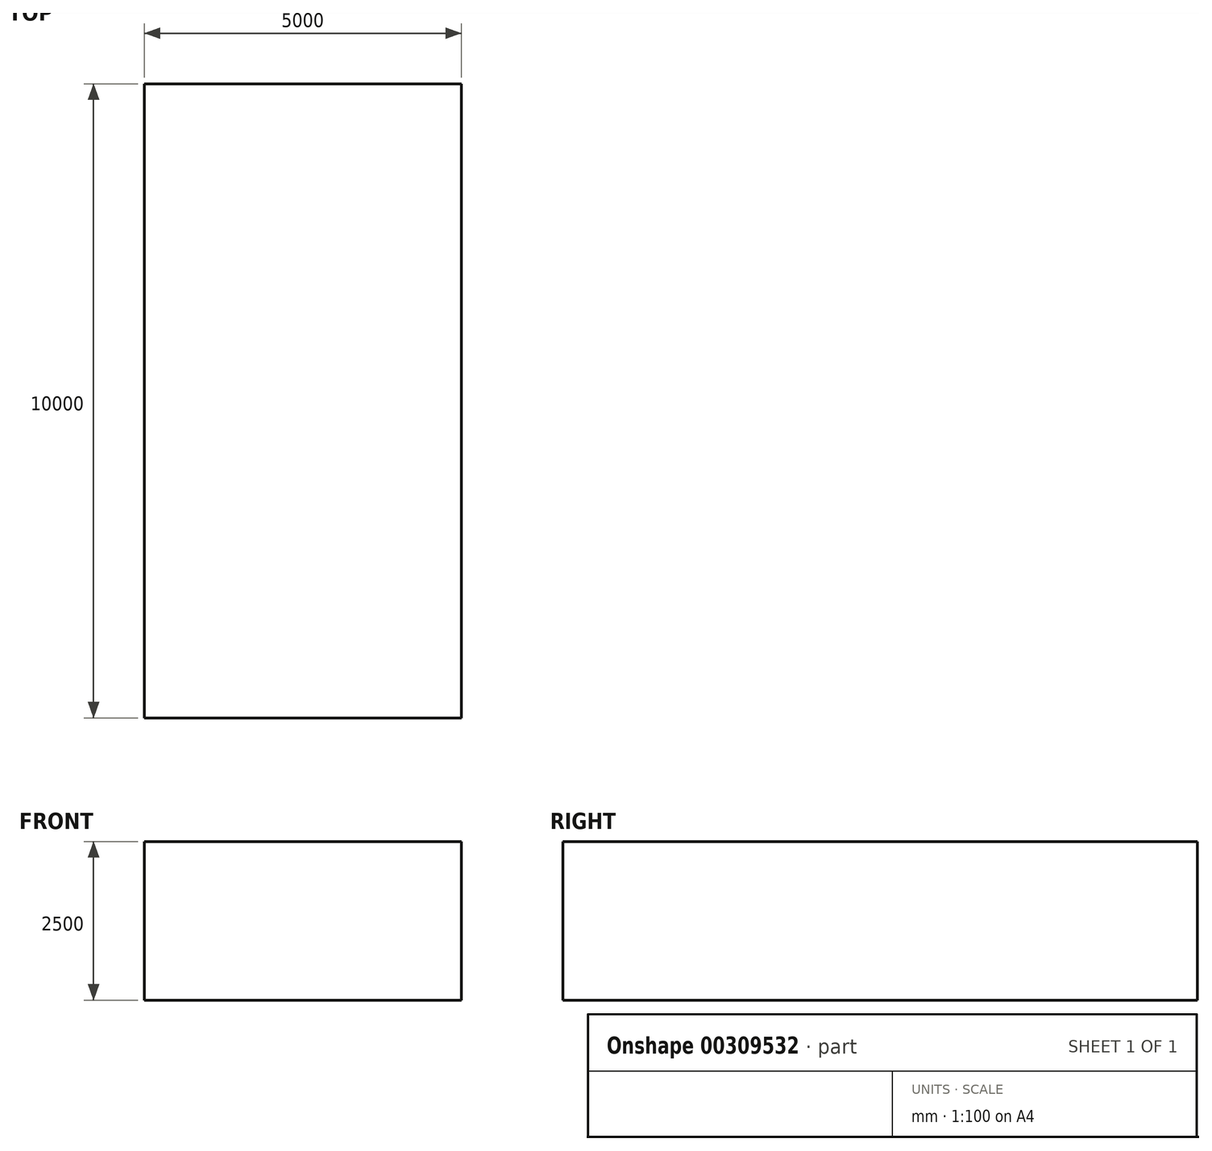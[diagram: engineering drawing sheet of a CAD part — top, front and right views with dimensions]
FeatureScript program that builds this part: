
annotation { "Feature Type Name" : "Feature", "Feature Type Description" : "" }
export const myFeature = defineFeature(function(context is Context, id is Id, definition is map)
    precondition{}
    {
        {
            var Q0;
            Q0=qCreatedBy(makeId("Front.planeOp"),FACE);
            var sketch = newSketch(context, id + "F0", { "sketchPlane" : qUnion([Q0])});
            skLineSegment(sketch, "E0.bottom", {"start": v(2500, -1250) * mm, "end": v(-2500, -1250) * mm});
            skLineSegment(sketch, "E0.top", {"start": v(2500, 1250) * mm, "end": v(-2500, 1250) * mm});
            skLineSegment(sketch, "E0.left", {"start": v(2500, -1250) * mm, "end": v(2500, 1250) * mm});
            skLineSegment(sketch, "E0.right", {"start": v(-2500, -1250) * mm, "end": v(-2500, 1250) * mm});
            skPoint(sketch, "E0.middle", {"position": v(0, 0) * mm});
            skSolve(sketch);
        }
        {
            var Q0;
            Q0=makeQuery(id+"F0.imprint","IMPRINT",FACE,{"disambiguationData":[TD([[makeQuery(id+"F0.imprint","IMPRINT",EDGE,{"derivedFrom":sQuery(id+"F0.wireOp",EDGE,"E0.bottom")}),-1.0]])]});
            extrude(context, id + "F1", {"entities" : qUnion([Q0]), "depth" : 10000 * mm});
        }
    });
